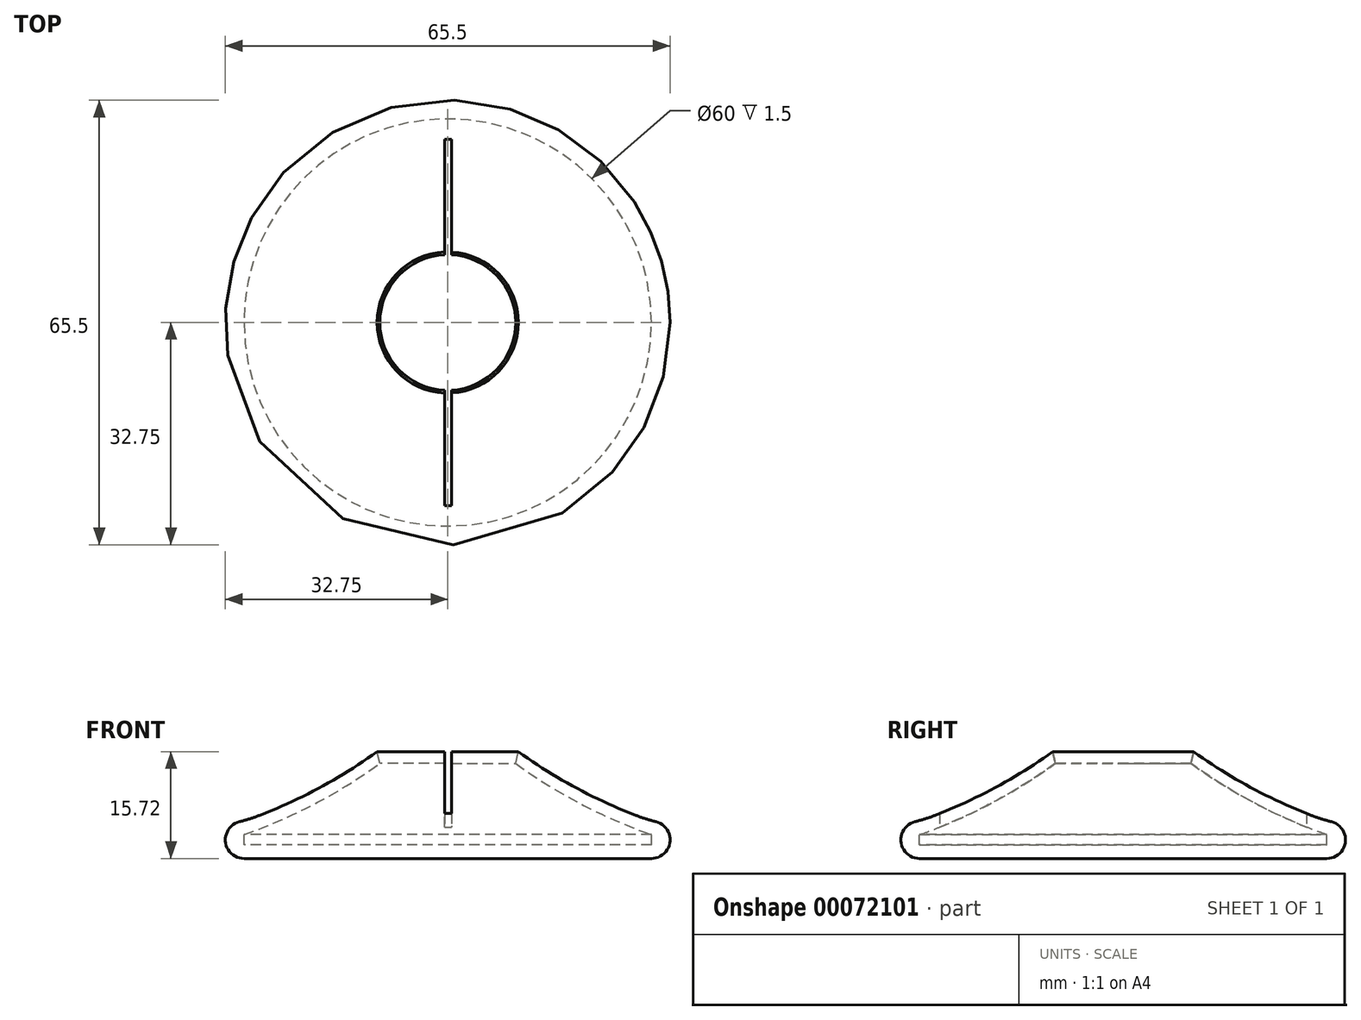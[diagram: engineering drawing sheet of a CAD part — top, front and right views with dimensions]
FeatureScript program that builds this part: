
annotation { "Feature Type Name" : "Feature", "Feature Type Description" : "" }
export const myFeature = defineFeature(function(context is Context, id is Id, definition is map)
    precondition{}
    {
        {
            var Q0;
            Q0=qCreatedBy(makeId("Front.planeOp"),FACE);
            var sketch = newSketch(context, id + "F0", { "sketchPlane" : qUnion([Q0])});
            skLineSegment(sketch, "E0", {"start": v(0, 0) * mm, "end": v(-14, 0) * mm, "construction": true});
            skLineSegment(sketch, "E1", {"start": v(-7, 0) * mm, "end": v(-7, -3.4) * mm, "construction": true});
            skLineSegment(sketch, "E2", {"start": v(23, -9.5) * mm, "end": v(23, -11) * mm});
            skLineSegment(sketch, "E3", {"start": v(23, -11) * mm, "end": v(-7, -11) * mm});
            skLineSegment(sketch, "E4", {"start": v(-7, -11) * mm, "end": v(-7, -13) * mm});
            skLineSegment(sketch, "E5", {"start": v(-7, -13) * mm, "end": v(23, -13) * mm});
            skArc(sketch, "E6", {"start": v(23, -13) * mm, "mid": v(25.75, -10.25) * mm, "end": v(23, -7.5) * mm});
            skArc(sketch, "E7", {"start": v(3, 1) * mm, "mid": v(12.62, -4.97) * mm, "end": v(23, -9.5) * mm});
            skLineSegment(sketch, "E8", {"start": v(3, 1) * mm, "end": v(3, 3) * mm});
            skArc(sketch, "E9", {"start": v(3, 3) * mm, "mid": v(12.62, -2.97) * mm, "end": v(23, -7.5) * mm});
            skSolve(sketch);
        }
        {
            var Q0;
            {var subQ4=sQuery(id+"F0.wireOp",EDGE,"E2");Q0=makeQuery(id+"F0.imprint","IMPRINT",FACE,{"disambiguationData":[TD([[makeQuery(id+"F0.imprint","IMPRINT",EDGE,{"derivedFrom":subQ4}),1.0]])]});}
            var Q1;
            Q1=sQuery(id+"F0.wireOp",EDGE,"E1");
            revolve(context, id + "F1", {"entities" : qUnion([Q0]), "axis" : qUnion([Q1]), "revolveType" : RevolveType.ONE_DIRECTION, "angle" : 360 * degree});
        }
        {
            var Q0;
            Q0=makeQuery(id+"F1.opRevolve","SWEPT_EDGE",EDGE,{"disambiguationData":[OSD([sQuery(id+"F0.wireOp",EDGE,"E8"),sQuery(id+"F0.wireOp",EDGE,"E9")])]});
            chamfer(context, id + "F2", {"entities" : qUnion([Q0]), "chamferType" : ChamferType.TWO_OFFSETS, "width1" : .5 * mm, "oppositeDirection" : true, "width2" : 2 * mm, "tangentPropagation" : true});
        }
        {
            var Q0;
            Q0=makeQuery(id+"F1.opRevolve","SWEPT_EDGE",EDGE,{"disambiguationData":[OSD([sQuery(id+"F0.wireOp",EDGE,"E6"),sQuery(id+"F0.wireOp",EDGE,"E9")])]});
            fillet(context, id + "F3", {"entities" : qUnion([Q0]), "radius" : 25 * mm, "tangentPropagation" : true, "allowEdgeOverflow" : false});
        }
        {
            var Q0;
            Q0=makeQuery(id+"F1.opRevolve","SWEPT_FACE",FACE,{"disambiguationData":[OSD([sQuery(id+"F0.wireOp",EDGE,"E5")])]});
            var sketch = newSketch(context, id + "F4", { "sketchPlane" : qUnion([Q0])});
            skLineSegment(sketch, "E10", {"start": v(-6.44, -27) * mm, "end": v(-6.44, 27) * mm});
            skLineSegment(sketch, "E11", {"start": v(-6.44, 27) * mm, "end": v(-7.44, 27) * mm});
            skLineSegment(sketch, "E12", {"start": v(-7.44, 27) * mm, "end": v(-7.44, -27) * mm});
            skLineSegment(sketch, "E13", {"start": v(-6.44, -27) * mm, "end": v(-7.44, -27) * mm});
            skLineSegment(sketch, "E14", {"start": v(-6.94, -30) * mm, "end": v(23, 0) * mm, "construction": true});
            skLineSegment(sketch, "E15", {"start": v(23, 0) * mm, "end": v(-7.06, 30) * mm, "construction": true});
            skLineSegment(sketch, "E16", {"start": v(-7.06, 30) * mm, "end": v(-37, 0) * mm, "construction": true});
            skLineSegment(sketch, "E17", {"start": v(-37, 0) * mm, "end": v(-6.94, -30) * mm, "construction": true});
            skLineSegment(sketch, "E18", {"start": v(-6.94, -27) * mm, "end": v(-6.94, -30) * mm, "construction": true});
            skSolve(sketch);
        }
        {
            var Q0;
            Q0=makeQuery(id+"F4.imprint","IMPRINT",FACE,{"disambiguationData":[TD([[makeQuery(id+"F4.imprint","IMPRINT",EDGE,{"derivedFrom":sQuery(id+"F4.wireOp",EDGE,"E10")}),1.0]])]});
            extrude(context, id + "F5", {"entities" : qUnion([Q0]), "operationType" : NewBodyOperationType.REMOVE, "oppositeDirection" : true, "depth" : 25 * mm, "hasSecondDirection" : true, "secondDirectionOppositeDirection" : true, "secondDirectionDepth" : 2.7 * mm});
        }
    });
